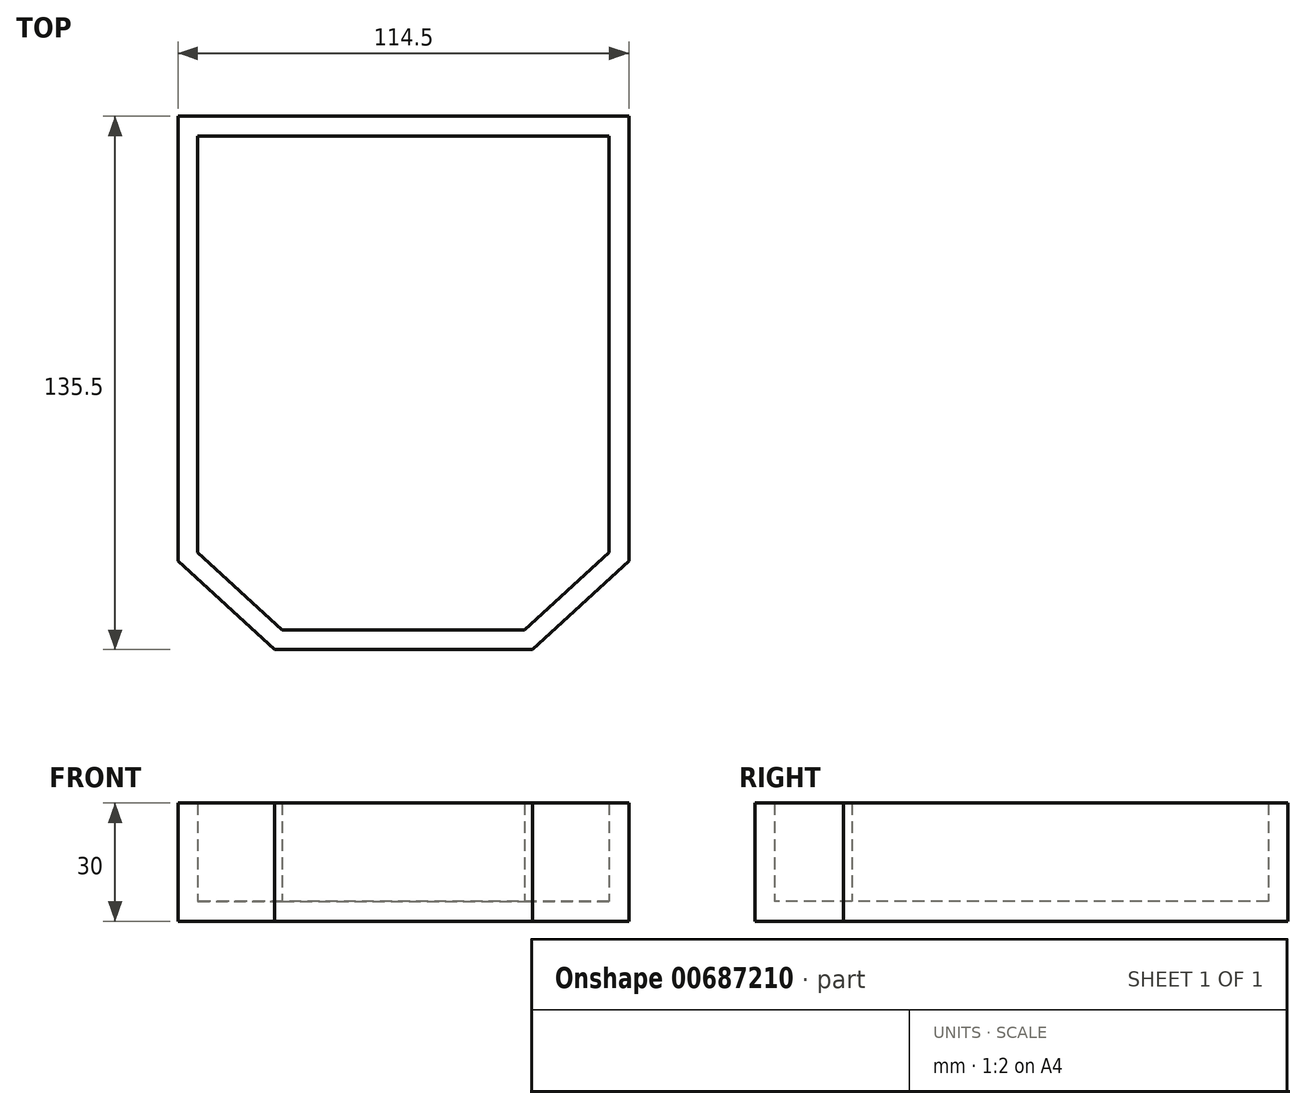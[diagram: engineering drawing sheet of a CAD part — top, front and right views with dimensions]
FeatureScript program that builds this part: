
annotation { "Feature Type Name" : "Feature", "Feature Type Description" : "" }
export const myFeature = defineFeature(function(context is Context, id is Id, definition is map)
    precondition{}
    {
        {
            var Q0;
            Q0=qCreatedBy(makeId("Top.planeOp"),FACE);
            var sketch = newSketch(context, id + "F0", { "sketchPlane" : qUnion([Q0])});
            skLineSegment(sketch, "E0.bottom", {"start": v(-64.2, 139.53) * mm, "end": v(50.3, 139.53) * mm});
            skLineSegment(sketch, "E0.top", {"start": v(-64.2, 4.03) * mm, "end": v(50.3, 4.03) * mm});
            skLineSegment(sketch, "E0.left", {"start": v(-64.2, 139.53) * mm, "end": v(-64.2, 4.03) * mm});
            skLineSegment(sketch, "E0.right", {"start": v(50.3, 139.53) * mm, "end": v(50.3, 4.03) * mm});
            skLineSegment(sketch, "E1", {"start": v(-64.2, 26.53) * mm, "end": v(-39.7, 4.03) * mm});
            skLineSegment(sketch, "E2", {"start": v(50.3, 26.53) * mm, "end": v(25.8, 4.03) * mm});
            skSolve(sketch);
        }
        {
            var Q0;
            {var subQ1=sQuery(id+"F0.wireOp",EDGE,"E0.bottom");Q0=makeQuery(id+"F0.imprint","IMPRINT",FACE,{"disambiguationData":[TD([[makeQuery(id+"F0.imprint","IMPRINT",EDGE,{"derivedFrom":subQ1}),-1.0]])]});}
            extrude(context, id + "F1", {"entities" : qUnion([Q0]), "depth" : 5 * mm, "offsetDistance" : 25 * mm});
        }
        {
            var Q0;
            Q0=makeQuery(id+"F1.opExtrude","CAP_FACE",FACE,{"disambiguationData":[OSD([sQuery(id+"F0.wireOp",EDGE,"E0.bottom"),sQuery(id+"F0.wireOp",EDGE,"E0.top"),sQuery(id+"F0.wireOp",EDGE,"E0.left"),sQuery(id+"F0.wireOp",EDGE,"E0.right"),sQuery(id+"F0.wireOp",EDGE,"E1"),sQuery(id+"F0.wireOp",EDGE,"E2")])],"isStart":false});
            var sketch = newSketch(context, id + "F2", { "sketchPlane" : qUnion([Q0])});
            skLineSegment(sketch, "E3.0", {"start": v(-59.2, 134.53) * mm, "end": v(-59.2, 28.73) * mm});
            skLineSegment(sketch, "E3.1", {"start": v(-37.76, 9.03) * mm, "end": v(23.85, 9.03) * mm});
            skLineSegment(sketch, "E3.2", {"start": v(23.85, 9.03) * mm, "end": v(45.3, 28.73) * mm});
            skLineSegment(sketch, "E3.3", {"start": v(-59.2, 28.73) * mm, "end": v(-37.76, 9.03) * mm});
            skLineSegment(sketch, "E3.4", {"start": v(45.3, 28.73) * mm, "end": v(45.3, 134.53) * mm});
            skLineSegment(sketch, "E3.5", {"start": v(45.3, 134.53) * mm, "end": v(-59.2, 134.53) * mm});
            skSolve(sketch);
        }
        {
            var Q0;
            Q0=makeQuery(id+"F2.imprint","IMPRINT",FACE,{"disambiguationData":[TD([[makeQuery(id+"F2.imprint","IMPRINT",EDGE,{"derivedFrom":sQuery(id+"F2.wireOp",EDGE,"E3.0")}),-1.0]])]});
            extrude(context, id + "F3", {"entities" : qUnion([Q0]), "operationType" : NewBodyOperationType.ADD, "depth" : 25 * mm, "offsetDistance" : 25 * mm});
        }
    });
